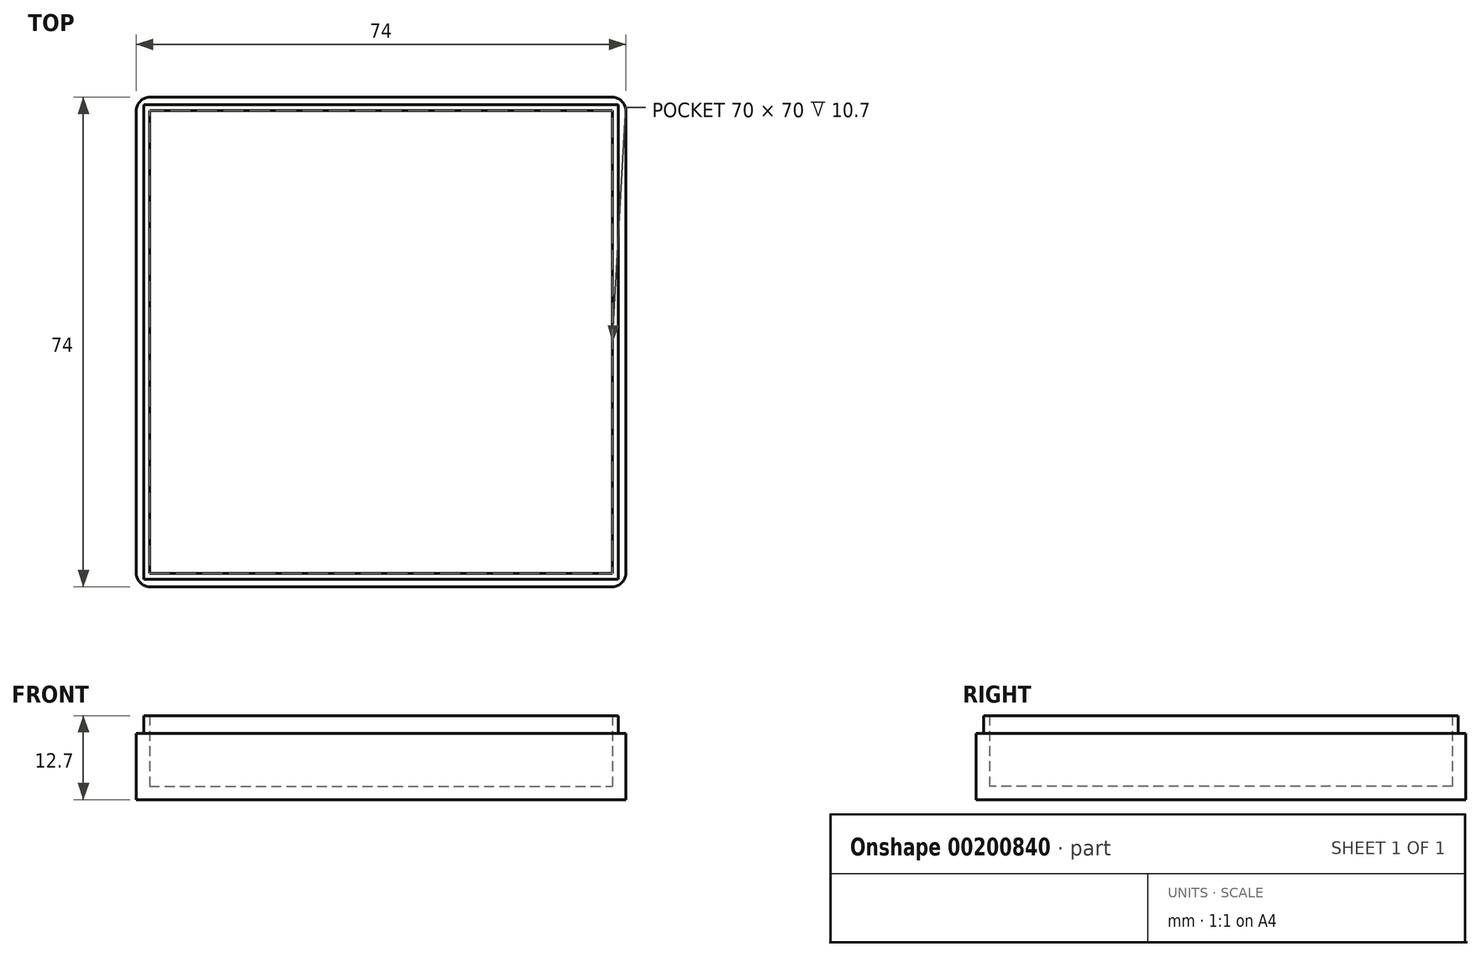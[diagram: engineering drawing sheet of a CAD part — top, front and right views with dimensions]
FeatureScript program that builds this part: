
annotation { "Feature Type Name" : "Feature", "Feature Type Description" : "" }
export const myFeature = defineFeature(function(context is Context, id is Id, definition is map)
    precondition{}
    {
        {
            var Q0;
            Q0=qCreatedBy(makeId("Top.planeOp"),FACE);
            var sketch = newSketch(context, id + "F0", { "sketchPlane" : qUnion([Q0])});
            skLineSegment(sketch, "E0.bottom", {"start": v(-39, 35) * mm, "end": v(35, 35) * mm});
            skLineSegment(sketch, "E0.top", {"start": v(-39, -39) * mm, "end": v(35, -39) * mm});
            skLineSegment(sketch, "E0.left", {"start": v(-39, 35) * mm, "end": v(-39, -39) * mm});
            skLineSegment(sketch, "E0.right", {"start": v(35, 35) * mm, "end": v(35, -39) * mm});
            skLineSegment(sketch, "E1.bottom", {"start": v(-37, 33) * mm, "end": v(33, 33) * mm});
            skLineSegment(sketch, "E1.top", {"start": v(-37, -37) * mm, "end": v(33, -37) * mm});
            skLineSegment(sketch, "E1.left", {"start": v(-37, 33) * mm, "end": v(-37, -37) * mm});
            skLineSegment(sketch, "E1.right", {"start": v(33, 33) * mm, "end": v(33, -37) * mm});
            skSolve(sketch);
        }
        {
            var Q0;
            Q0=makeQuery(id+"F0.imprint","IMPRINT",FACE,{"disambiguationData":[TD([[makeQuery(id+"F0.imprint","IMPRINT",EDGE,{"derivedFrom":sQuery(id+"F0.wireOp",EDGE,"E0.bottom")}),-1.0]])]});
            extrude(context, id + "F1", {"entities" : qUnion([Q0]), "depth" : 10 * mm});
        }
        {
            var Q0;
            Q0=makeQuery(id+"F0.imprint","IMPRINT",FACE,{"disambiguationData":[TD([[makeQuery(id+"F0.imprint","IMPRINT",EDGE,{"derivedFrom":sQuery(id+"F0.wireOp",EDGE,"E1.bottom")}),-1.0]])]});
            extrude(context, id + "F2", {"entities" : qUnion([Q0]), "operationType" : NewBodyOperationType.ADD, "depth" : 2 * mm});
        }
        {
            var Q0;
            Q0=makeQuery(id+"F1.opExtrude","CAP_FACE",FACE,{"disambiguationData":[OSD([sQuery(id+"F0.wireOp",EDGE,"E0.bottom"),sQuery(id+"F0.wireOp",EDGE,"E0.top"),sQuery(id+"F0.wireOp",EDGE,"E0.left"),sQuery(id+"F0.wireOp",EDGE,"E0.right"),sQuery(id+"F0.wireOp",EDGE,"E1.bottom"),sQuery(id+"F0.wireOp",EDGE,"E1.top"),sQuery(id+"F0.wireOp",EDGE,"E1.left"),sQuery(id+"F0.wireOp",EDGE,"E1.right")])],"isStart":false});
            var sketch = newSketch(context, id + "F3", { "sketchPlane" : qUnion([Q0])});
            skLineSegment(sketch, "E2.bottom", {"start": v(-37, 33) * mm, "end": v(33, 33) * mm});
            skLineSegment(sketch, "E2.top", {"start": v(-37, -37) * mm, "end": v(33, -37) * mm});
            skLineSegment(sketch, "E2.left", {"start": v(-37, 33) * mm, "end": v(-37, -37) * mm});
            skLineSegment(sketch, "E2.right", {"start": v(33, 33) * mm, "end": v(33, -37) * mm});
            skLineSegment(sketch, "E3.bottom", {"start": v(-37.9, 33.9) * mm, "end": v(33.9, 33.9) * mm});
            skLineSegment(sketch, "E3.top", {"start": v(-37.9, -37.9) * mm, "end": v(33.9, -37.9) * mm});
            skLineSegment(sketch, "E3.left", {"start": v(-37.9, 33.9) * mm, "end": v(-37.9, -37.9) * mm});
            skLineSegment(sketch, "E3.right", {"start": v(33.9, 33.9) * mm, "end": v(33.9, -37.9) * mm});
            skSolve(sketch);
        }
        {
            var Q0;
            Q0=makeQuery(id+"F3.imprint","IMPRINT",FACE,{"disambiguationData":[TD([[makeQuery(id+"F3.imprint","IMPRINT",EDGE,{"derivedFrom":sQuery(id+"F3.wireOp",EDGE,"E2.bottom")}),1.0]])]});
            extrude(context, id + "F4", {"entities" : qUnion([Q0]), "operationType" : NewBodyOperationType.ADD, "depth" : 2.7 * mm});
        }
        {
            var Q0;
            Q0=makeQuery(id+"F1.opExtrude","SWEPT_EDGE",EDGE,{"disambiguationData":[OSD([sQuery(id+"F0.wireOp",EDGE,"E0.top"),sQuery(id+"F0.wireOp",EDGE,"E0.left")])]});
            var Q1;
            Q1=makeQuery(id+"F1.opExtrude","SWEPT_EDGE",EDGE,{"disambiguationData":[OSD([sQuery(id+"F0.wireOp",EDGE,"E0.top"),sQuery(id+"F0.wireOp",EDGE,"E0.right")])]});
            var Q2;
            Q2=makeQuery(id+"F1.opExtrude","SWEPT_EDGE",EDGE,{"disambiguationData":[OSD([sQuery(id+"F0.wireOp",EDGE,"E0.bottom"),sQuery(id+"F0.wireOp",EDGE,"E0.right")])]});
            var Q3;
            Q3=makeQuery(id+"F1.opExtrude","SWEPT_EDGE",EDGE,{"disambiguationData":[OSD([sQuery(id+"F0.wireOp",EDGE,"E0.bottom"),sQuery(id+"F0.wireOp",EDGE,"E0.left")])]});
            fillet(context, id + "F5", {"entities" : qUnion([Q0, Q1, Q2, Q3]), "radius" : 2 * mm, "tangentPropagation" : true, "allowEdgeOverflow" : false});
        }
    });
